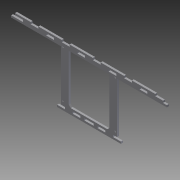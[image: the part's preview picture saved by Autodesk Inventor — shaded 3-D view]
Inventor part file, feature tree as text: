
AUTODESK INVENTOR PART (.ipt)
format: ipt  version: 2011 (Build 150239000, 239)  size: 641,536 bytes
history: native  units: in
note: dims shown in document units (in); Inventor stores cm internally (conversion verified against a paired STEP export)
features: extrude x23, sketch x23, fillet x2
ambient origin geometry x8: Origin, YZ Plane, XZ Plane, XY Plane, X Axis, Y Axis, Z Axis, Center Point
bodies: Solid1 (feature_tree)
feature tree (48):
  extrude  "Extrusion1"  Depth=41.5in
  extrude  "Extrusion2"  Depth=10.0in
  extrude  "Extrusion3"  Depth=0.6in
  extrude  "Extrusion4"  Depth=0.25in
  extrude  "Extrusion5"  Depth=0.5in
  extrude  "Extrusion6"  Depth=1.0in
  extrude  "Extrusion7"  Depth=4.1in TaperAngle=0.0deg
  extrude  "Extrusion8"  Depth=1.0in
  extrude  "Extrusion9"  Depth=1.0in
  extrude  "Extrusion10"  Depth=1.0in
  extrude  "Extrusion11"  Depth=4.1in TaperAngle=0.0deg
  extrude  "Extrusion12"  Depth=0.5in
  fillet  "Fillet1"  Radius=0.25in
  fillet  "Fillet2"  Radius=1.0in
  extrude  "Extrusion13"  Depth=3.0in
  extrude  "Extrusion14"  Depth=3.0in
  extrude  "Extrusion15"  Depth=3.0in
  extrude  "Extrusion16"  Depth=3.0in
  extrude  "Extrusion17"  Depth=3.0in
  extrude  "Extrusion18"  Depth=0.25in
  extrude  "Extrusion19"  Depth=0.25in TaperAngle=0.0deg
  extrude  "Extrusion20"  Depth=0.25in
  extrude  "Extrusion21"  Depth=1.0in
  extrude  "Extrusion22"  Depth=1.0in
  extrude  "Extrusion23"  Depth=0.156in
  sketch  "Sketch1"  dims[d0=20.0in d1=41.5in]
  sketch  "Sketch2"  dims[d2=0.25in d3=0.0in d4=10.0in]
  sketch  "Sketch3"  dims[d5=0.25in d6=0.6in]
  sketch  "Sketch4"  dims[d7=1.2in d8=0.25in]
  sketch  "Sketch5"  dims[d9=4.1in d10=0.0in d11=0.5in]
  sketch  "Sketch6"  dims[d12=0.5in d13=1.0in]
  sketch  "Sketch7"  dims[d14=1.0in d15=4.1in d16=0.0in]
  sketch  "Sketch8"  dims[d17=1.0in d18=1.0in]
  sketch  "Sketch9"  dims[d19=1.0in d20=1.0in]
  sketch  "Sketch10"  dims[d21=6.75in d22=1.0in]
  sketch  "Sketch11"  dims[d23=0.5in d24=4.1in d25=0.0in]
  sketch  "Sketch12"  dims[d26=0.25in d27=0.5in d28=0.25in d29=0.0in d30=1.0in]
  sketch  "Sketch13"  dims[d31=1.0in d32=3.0in]
  sketch  "Sketch14"  dims[d33=1.0in d34=3.0in]
  sketch  "Sketch15"  dims[d35=1.0in d36=3.0in]
  sketch  "Sketch16"  dims[d37=1.0in d38=3.0in]
  sketch  "Sketch17"  dims[d39=1.0in d40=3.0in]
  sketch  "Sketch18"  dims[d41=1.0in d42=0.25in]
  sketch  "Sketch19"  dims[d43=1.0in d44=0.0in d45=0.25in d46=0.0in]
  sketch  "Sketch20"  dims[d47=1.0in d48=0.25in]
  sketch  "Sketch21"  dims[d49=1.0in d50=1.0in]
  sketch  "Sketch22"  dims[d51=1.0in d52=1.0in]
  sketch  "Sketch23"  dims[d53=0.25in d54=0.0in d55=0.156in d56=0.156in d57=0.156in d58=0.156in d59=0.25in d60=0.0in d61=0.25in d62=0.0in d63=0.25in d64=0.0in d65=1.0in d66=1.0in d67=1.0in d68=1.0in d69=1.0in d70=1.0in d71=1.0in d72=1.0in d73=0.25in d74=0.0in d75=0.5in d76=0.5in d77=1.0in d78=0.0in d79=3.0in d80=3.0in d81=0.25in d82=0.0in d83=0.75in d84=0.75in d85=0.75in d86=0.75in d87=0.156in d88=0.156in d89=0.25in d90=0.0in d91=0.25in d92=1.0in d93=1.0in d94=1.0in d95=0.25in d96=0.0in d97=0.25in d98=1.0in d99=1.0in d100=1.0in d101=0.25in d102=0.0in d103=1.0in d104=0.0in d105=0.75in d106=0.5in d107=0.156in d108=0.156in d109=1.0in d110=0.0in d111=0.25in d112=0.0in d113=0.5in d114=0.5in d115=1.0in d116=0.25in d117=1.0in d118=1.0in d119=1.0in d120=1.0in d121=1.0in d122=1.0in d123=1.0in d124=1.0in d125=1.0in d126=1.0in d127=1.0in d128=1.0in d129=1.0in d130=1.0in d131=1.0in d132=1.0in d133=1.0in d134=1.0in d135=0.25in d136=0.0in d137=0.25in d138=0.0in d139=1.0in d140=0.0in]
